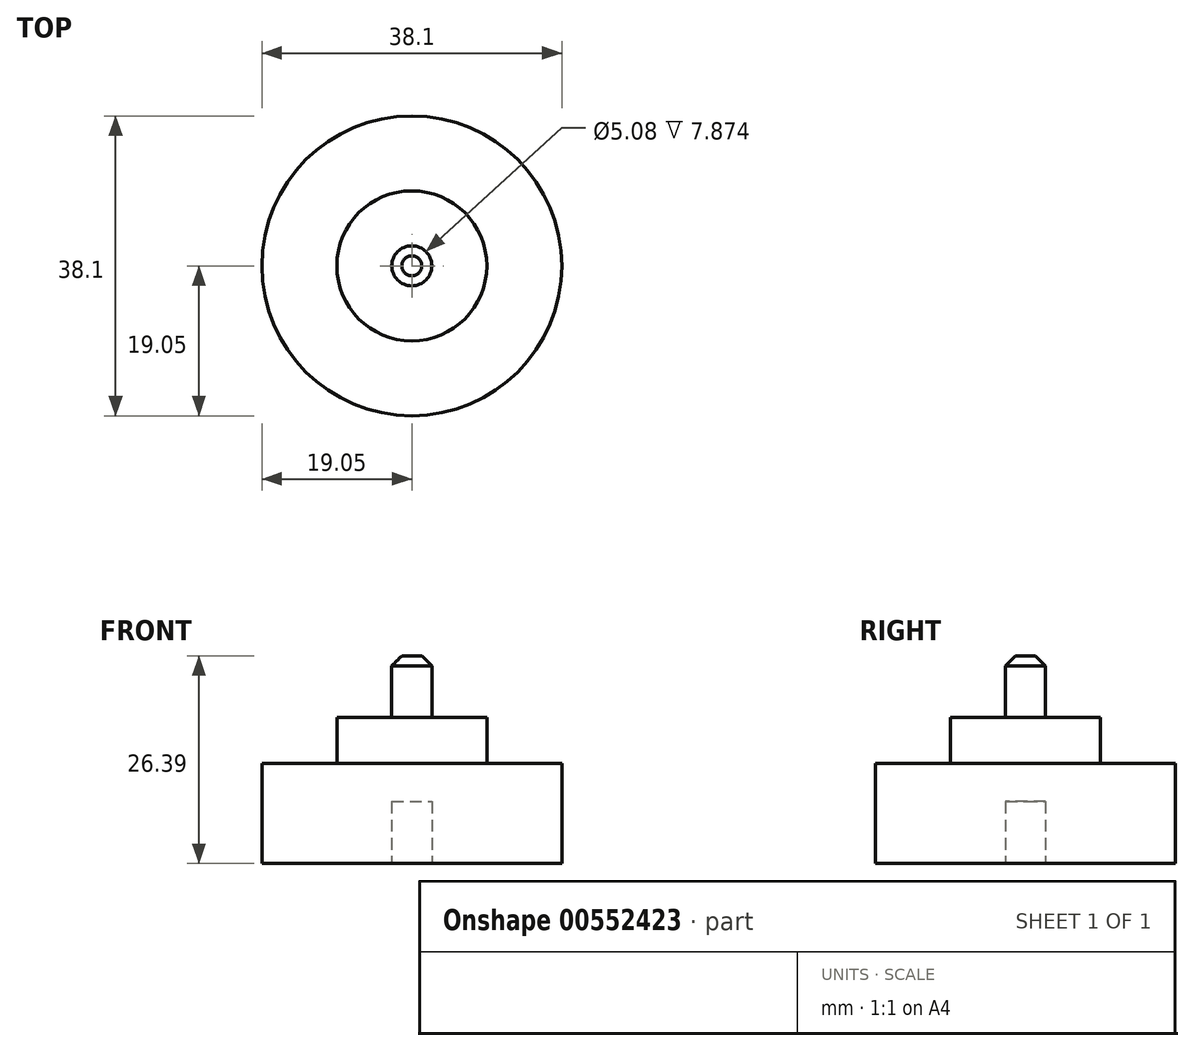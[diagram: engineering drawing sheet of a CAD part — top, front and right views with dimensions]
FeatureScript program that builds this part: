
annotation { "Feature Type Name" : "Feature", "Feature Type Description" : "" }
export const myFeature = defineFeature(function(context is Context, id is Id, definition is map)
    precondition{}
    {
        {
            var Q0;
            Q0=qCreatedBy(makeId("Front.planeOp"),FACE);
            var sketch = newSketch(context, id + "F0", { "sketchPlane" : qUnion([Q0])});
            skLineSegment(sketch, "E0", {"start": v(19.05, 0) * mm, "end": v(19.05, 12.7) * mm});
            skLineSegment(sketch, "E1", {"start": v(19.05, 12.7) * mm, "end": v(9.53, 12.7) * mm});
            skLineSegment(sketch, "E2", {"start": v(2.54, 18.54) * mm, "end": v(9.53, 18.54) * mm});
            skPoint(sketch, "E2.endSnap0", {"position": v(9.53, 12.7) * mm});
            skLineSegment(sketch, "E3", {"start": v(9.53, 18.54) * mm, "end": v(9.53, 12.7) * mm});
            skLineSegment(sketch, "E4", {"start": v(0, 26.4) * mm, "end": v(2.54, 26.4) * mm});
            skLineSegment(sketch, "E5", {"start": v(2.54, 26.4) * mm, "end": v(2.54, 18.54) * mm});
            skPoint(sketch, "E6.start.orphan", {"position": v(0, 12.7) * mm});
            skLineSegment(sketch, "E7", {"start": v(2.54, 0) * mm, "end": v(2.54, 7.87) * mm});
            skLineSegment(sketch, "E8", {"start": v(2.54, 7.87) * mm, "end": v(0, 7.87) * mm});
            skLineSegment(sketch, "E9", {"start": v(0, 7.87) * mm, "end": v(0, 26.4) * mm});
            skLineSegment(sketch, "E10", {"start": v(2.54, 0) * mm, "end": v(19.05, 0) * mm});
            skSolve(sketch);
        }
        {
            var Q0;
            Q0 = qSketchRegion(id + "F0", true);
            var Q1;
            Q1=sQuery(id+"F0.wireOp",EDGE,"E9");
            revolve(context, id + "F1", {"entities" : qUnion([Q0]), "axis" : qUnion([Q1]), "revolveType" : RevolveType.FULL});
        }
        {
            var Q0;
            Q0=makeQuery(id+"F1.opRevolve","SWEPT_EDGE",EDGE,{"disambiguationData":[OSD([sQuery(id+"F0.wireOp",EDGE,"E4"),sQuery(id+"F0.wireOp",EDGE,"E5")])]});
            chamfer(context, id + "F2", {"entities" : qUnion([Q0]), "width" : 1.27 * mm, "tangentPropagation" : true});
        }
    });
